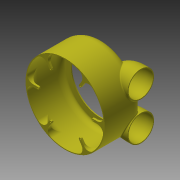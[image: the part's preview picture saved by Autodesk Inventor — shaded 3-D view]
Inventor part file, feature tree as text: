
AUTODESK INVENTOR PART (.ipt)
format: ipt  version: 2015 (Build 190159000, 159)  size: 797,184 bytes
history: native  units: mm
features: sketch x10, extrude x6, revolve x5, fillet x3
ambient origin geometry x8: Origin, YZ Plane, XZ Plane, XY Plane, X Axis, Y Axis, Z Axis, Center Point
bodies: Body1 (feature_tree)
feature tree (24):
  sketch  "Boceto1"  dims[d1=40.0mm d2=20.0mm d3=20.0mm d4=5.0mm d5=360.0deg d6=5.0mm d7=5.0mm d9=5.0mm d10=10.0mm d11=2.451216mm d13=270.0mm]
  revolve  "Revolución1"  [1 undecoded]
  sketch  "Boceto3"  dims[d20=3.0mm d21=120.0mm]
  extrude  "Extrusión2"  Depth=100.0mm
  extrude  "Extrusión3"  Depth=120.0mm
  sketch  "Boceto6"  dims[d22=3.0mm d23=120.0mm]
  revolve  "Revolución2"  [1 undecoded]
  revolve  "Revolución3"  [1 undecoded]
  revolve  "Revolución4"  [1 undecoded]
  revolve  "Revolución5"  [1 undecoded]
  fillet  "Empalme2"  Radius=100.0mm
  sketch  "Boceto7"  dims[d24=90.0deg]
  extrude  "Extrusión7"  Depth=20.0mm
  extrude  "Extrusión8"  Depth=20.0mm
  extrude  "Extrusión9"  TaperAngle=90.0deg  [1 undecoded]
  extrude  "Extrusión10"  TaperAngle=90.0deg  [1 undecoded]
  fillet  "Empalme4"  [1 undecoded]
  fillet  "Empalme5"  [1 undecoded]
  sketch  "Boceto16"  dims[d57=135.0mm d58=3.0mm d59=90.0deg d60=90.0deg d61=90.0deg d62=90.0deg d63=3.0mm d69=20.0mm d70=10.0mm d71=10.0mm d73=10.0mm d74=111.0mm d75=0.0mm d79=8.0mm d80=8.0mm d81=8.0mm d82=8.0mm d83=6.0mm d84=0.0mm d87=20.0mm d89=360.0deg d91=6.0mm d92=0.0mm d93=6.0mm d94=0.0mm d95=30.0mm d96=20.0mm d97=60.0deg]
  sketch  "Boceto2"  dims[d14=3.0mm d19=100.0mm]
  sketch  "Boceto11"  dims[d26=40.0mm d27=20.0mm d28=20.0mm d29=5.0mm d30=360.0deg d31=5.0mm d32=5.0mm d33=5.0mm d34=10.0mm d35=2.451216mm d36=270.0mm d37=3.0mm d38=60.0mm d39=0.0mm]
  sketch  "Boceto12"  dims[d40=3.0mm d41=0.0mm d51=20.0mm]
  sketch  "Boceto13"  dims[d52=45.0mm d53=20.0mm d54=100.0mm]
  sketch  "Boceto14"  dims[d55=90.0deg d56=20.0mm]
note: 9 required parameter values undecoded (feature->parameter linkage not recoverable at this tier; creation-order binding heuristic only, values carry confidence <= 0.55)